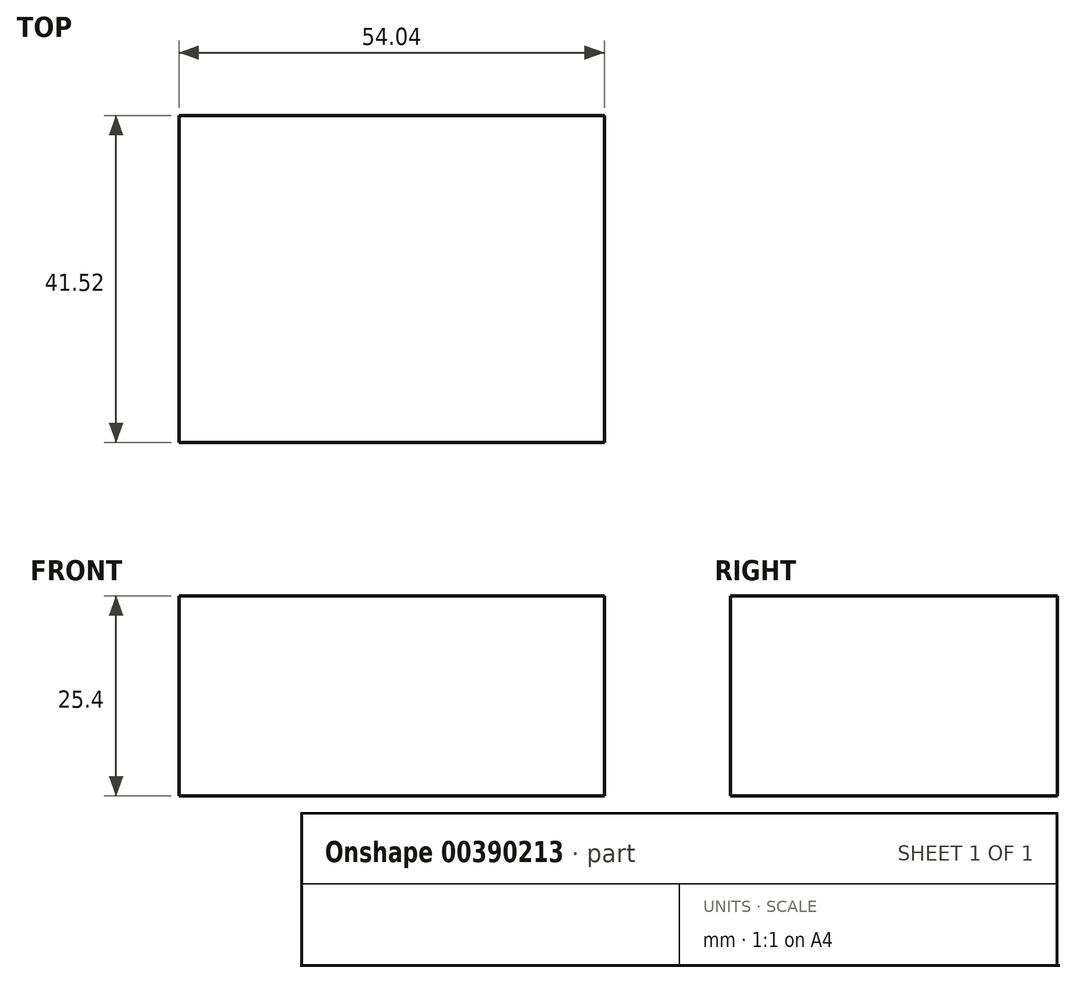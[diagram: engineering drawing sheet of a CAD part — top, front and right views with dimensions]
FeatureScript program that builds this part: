
annotation { "Feature Type Name" : "Feature", "Feature Type Description" : "" }
export const myFeature = defineFeature(function(context is Context, id is Id, definition is map)
    precondition{}
    {
        {
            var Q0;
            Q0=qCreatedBy(makeId("Top.planeOp"),FACE);
            var sketch = newSketch(context, id + "F0", { "sketchPlane" : qUnion([Q0])});
            skLineSegment(sketch, "E0.bottom", {"start": v(0, 0) * mm, "end": v(54.04, 0) * mm});
            skLineSegment(sketch, "E0.top", {"start": v(0, 41.52) * mm, "end": v(54.04, 41.52) * mm});
            skLineSegment(sketch, "E0.left", {"start": v(0, 0) * mm, "end": v(0, 41.52) * mm});
            skLineSegment(sketch, "E0.right", {"start": v(54.04, 0) * mm, "end": v(54.04, 41.52) * mm});
            skSolve(sketch);
        }
        {
            var Q0;
            Q0=makeQuery(id+"F0.imprint","IMPRINT",FACE,{"disambiguationData":[TD([[makeQuery(id+"F0.imprint","IMPRINT",EDGE,{"derivedFrom":sQuery(id+"F0.wireOp",EDGE,"E0.bottom")}),1.0]])]});
            extrude(context, id + "F1", {"entities" : qUnion([Q0]), "depth" : 25.4 * mm, "offsetDistance" : 25.4 * mm});
        }
        {
            var Q0;
            Q0=makeQuery(id+"F1.opExtrude","CAP_FACE",FACE,{"disambiguationData":[OSD([sQuery(id+"F0.wireOp",EDGE,"E0.bottom"),sQuery(id+"F0.wireOp",EDGE,"E0.top"),sQuery(id+"F0.wireOp",EDGE,"E0.left"),sQuery(id+"F0.wireOp",EDGE,"E0.right")])],"isStart":false});
            var sketch = newSketch(context, id + "F2", { "sketchPlane" : qUnion([Q0])});
            skCircle(sketch, "E1", {"center": v(38.23, 22.22) * mm, "radius": 9.27 * mm});
            skSolve(sketch);
        }
        {
            var Q0;
            Q0=makeQuery(id+"F2.imprint","IMPRINT",FACE,{"disambiguationData":[TD([[makeQuery(id+"F2.imprint","IMPRINT",EDGE,{"derivedFrom":sQuery(id+"F2.wireOp",EDGE,"E1")}),1.0]])]});
            extrude(context, id + "F3", {"entities" : qUnion([Q0]), "operationType" : NewBodyOperationType.ADD, "depth" : -25.4 * mm, "offsetDistance" : 25.4 * mm});
        }
    });
